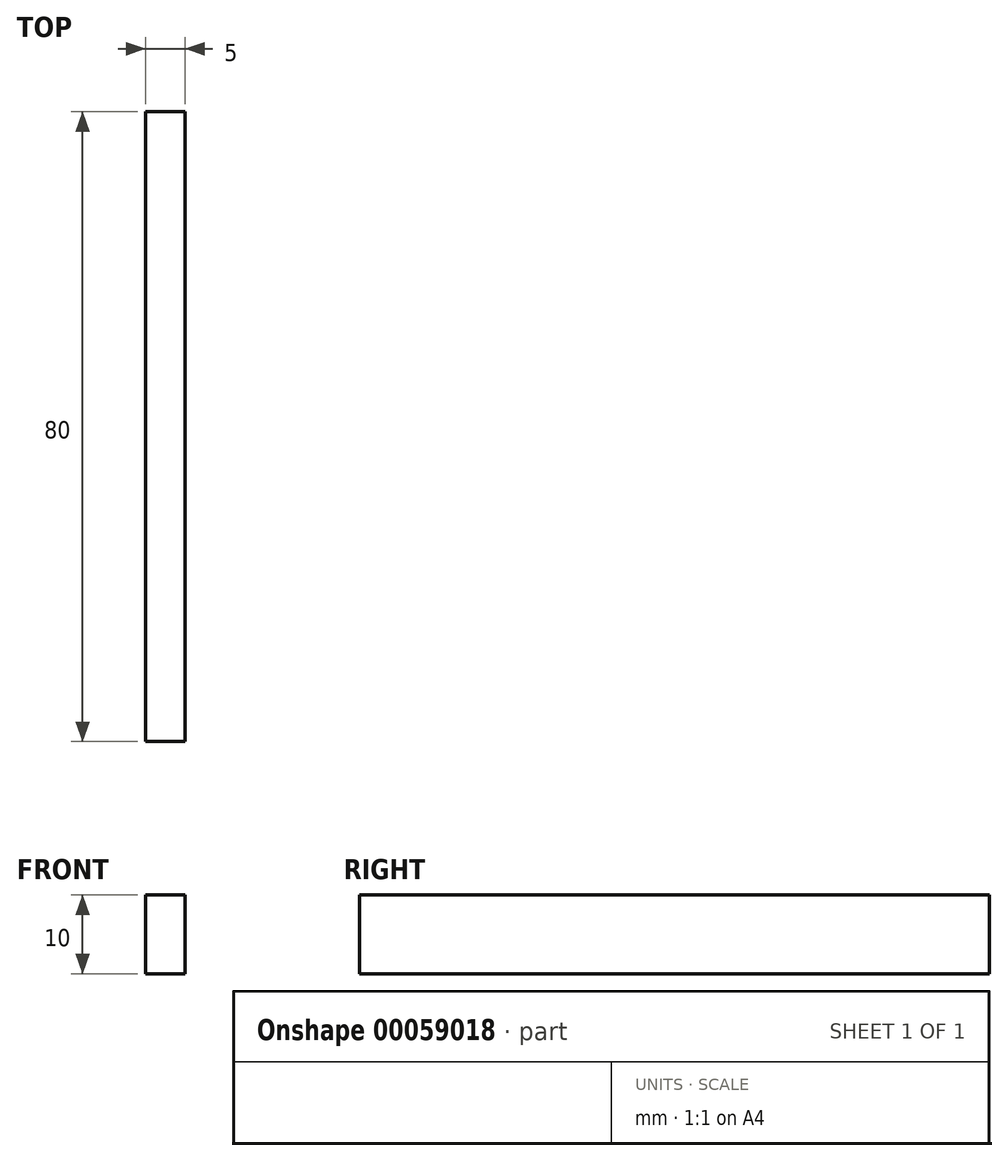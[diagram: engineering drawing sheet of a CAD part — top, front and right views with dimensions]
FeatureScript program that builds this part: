
annotation { "Feature Type Name" : "Feature", "Feature Type Description" : "" }
export const myFeature = defineFeature(function(context is Context, id is Id, definition is map)
    precondition{}
    {
        {
            var Q0;
            Q0=qCreatedBy(makeId("Top.planeOp"),FACE);
            var sketch = newSketch(context, id + "F0", { "sketchPlane" : qUnion([Q0])});
            skLineSegment(sketch, "E0.rect.bottom", {"start": v(-2.5, 40) * mm, "end": v(2.5, 40) * mm});
            skLineSegment(sketch, "E0.rect.top", {"start": v(-2.5, -40) * mm, "end": v(2.5, -40) * mm});
            skLineSegment(sketch, "E0.rect.left", {"start": v(-2.5, 40) * mm, "end": v(-2.5, -40) * mm});
            skLineSegment(sketch, "E0.rect.right", {"start": v(2.5, 40) * mm, "end": v(2.5, -40) * mm});
            skPoint(sketch, "E0.rect.middle", {"position": v(0, 0) * mm});
            skSolve(sketch);
        }
        {
            var Q0;
            Q0 = qSketchRegion(id + "F0", true);
            extrude(context, id + "F1", {"entities" : qUnion([Q0]), "depth" : 10 * mm});
        }
    });
